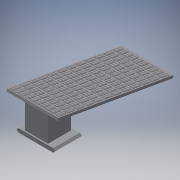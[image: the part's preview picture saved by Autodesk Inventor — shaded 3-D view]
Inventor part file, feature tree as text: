
AUTODESK INVENTOR PART (.ipt)
format: ipt  version: 2018.3 (Build 223284000, 284)  size: 1,254,912 bytes
history: native  units: mm
features: extrude x14, sketch x13, chamfer x6, pattern_linear x4
ambient origin geometry x8: Origin, YZ Plane, XZ Plane, XY Plane, X Axis, Y Axis, Z Axis, Center Point
bodies: Solid1 (feature_tree)
feature tree (37):
  extrude  "Extrusion1"  Depth=1.8mm
  extrude  "Extrusion2"  Depth=1.5mm TaperAngle=0.0deg
  chamfer  "Chamfer2"  Distance=10.0mm
  chamfer  "Chamfer3"  Distance=1.0mm
  extrude  "Extrusion3"  Depth=1.0mm TaperAngle=0.0deg
  extrude  "Extrusion4"  Depth=18.0mm
  extrude  "Extrusion5"  Depth=9.0mm
  pattern_linear  "Rectangular Pattern1"  Spacing1=9.0mm  [1 undecoded]
  pattern_linear  "Rectangular Pattern2"  Spacing1=6.788202mm  [1 undecoded]
  extrude  "Extrusion6"  Depth=1.4mm
  chamfer  "Chamfer7"  Distance=3.0mm
  chamfer  "Chamfer8"  Distance=0.5mm
  chamfer  "Chamfer9"  Distance=0.5mm
  chamfer  "Chamfer10"  Distance=0.2mm
  extrude  "Extrusion7"  Depth=0.2mm
  extrude  "Extrusion8"  Depth=0.5mm
  extrude  "Extrusion9"  Depth=0.25mm
  extrude  "Extrusion10"  Depth=0.25mm
  extrude  "Extrusion11"  Depth=0.2mm TaperAngle=0.0deg
  extrude  "Extrusion12"  Depth=0.2mm
  extrude  "Extrusion13"  Depth=0.2mm
  extrude  "Extrusion14"  Depth=0.5mm
  pattern_linear  "Rectangular Pattern3"  Spacing1=0.25mm  [1 undecoded]
  pattern_linear  "Rectangular Pattern4"  Spacing1=0.25mm  [1 undecoded]
  sketch  "Sketch2"  dims[d0=1.8mm d2=15.0mm]
  sketch  "Sketch3"  dims[d3=5.5mm d6=1.5mm d7=0.0mm]
  sketch  "Sketch4"  dims[d8=0.5mm]
  sketch  "Sketch5"  dims[d9=3.0mm]
  sketch  "Sketch6"  dims[d10=0.5mm]
  sketch  "Sketch7"  dims[d11=2.0mm]
  sketch  "Sketch8"  dims[d12=0.5mm]
  sketch  "Sketch9"  dims[d13=1.5mm]
  sketch  "Sketch10"  dims[d14=6.25mm]
  sketch  "Sketch11"  dims[d15=6.25mm d16=10.0mm d17=0.0mm d21=0.52mm d22=1.0mm d23=13.962634mm]
  sketch  "Sketch12"  dims[d24=0.52mm d25=1.0mm d26=13.962634mm d27=1.0mm d28=0.0mm]
  sketch  "Sketch13"  dims[d29=18.0mm d30=18.0mm]
  sketch  "Sketch14"  dims[d31=48.5mm d32=9.0mm d33=9.0mm d34=6.788202mm d35=1.4mm d36=3.0mm d37=0.5mm d38=0.5mm d39=0.2mm d40=0.2mm d41=0.5mm d42=0.25mm d43=0.25mm d44=0.2mm d45=0.0mm d46=0.2mm d47=0.2mm d48=0.5mm d49=0.25mm d50=0.25mm d51=0.1mm d52=0.0mm d53=90.0mm d55=1.95mm d56=120.0mm d58=3.7mm d59=10.0mm d60=0.0mm d70=0.75mm d71=2.0mm d72=45.0deg d73=0.75mm d74=2.0mm d75=45.0deg d76=0.75mm d77=2.0mm d78=45.0deg d79=0.75mm d80=2.0mm d81=45.0deg d86=3.0mm d87=0.0mm d88=3.0mm d89=0.0mm d90=5.0mm d91=0.0mm d92=1.0mm d93=0.0mm d94=5.0mm d95=0.0mm d96=9.0mm d97=0.0mm d98=2.0mm d99=0.0mm d100=3.0mm d101=0.0mm d102=20.0mm d104=1.95mm d105=120.0mm d107=3.7mm]
note: 4 required parameter values undecoded (feature->parameter linkage not recoverable at this tier; creation-order binding heuristic only, values carry confidence <= 0.55)
